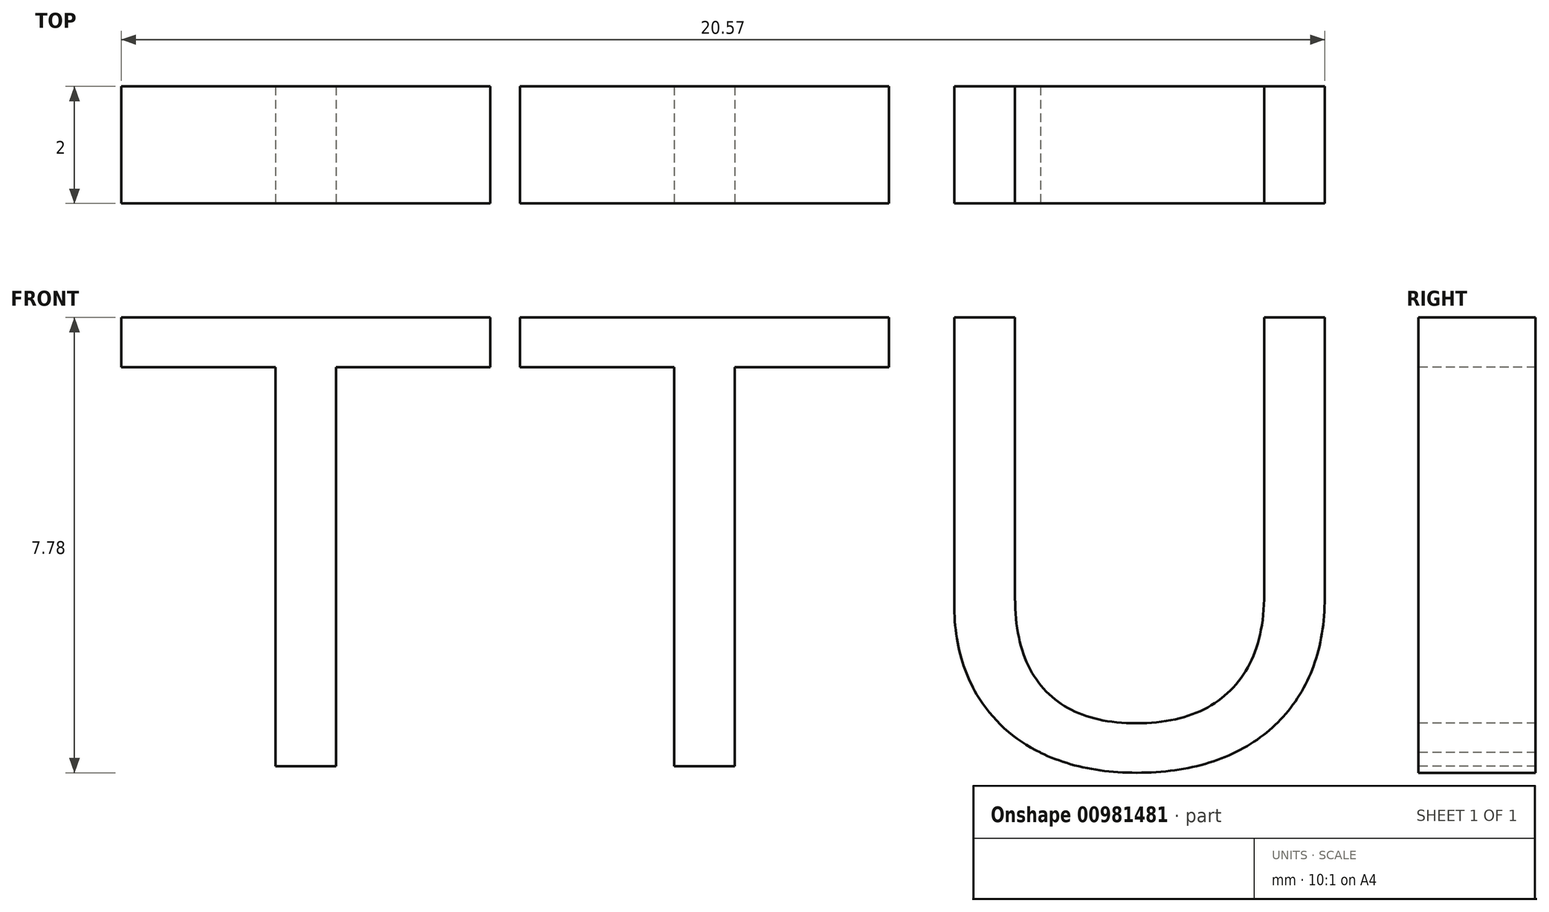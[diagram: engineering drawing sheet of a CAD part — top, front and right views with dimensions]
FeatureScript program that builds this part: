
annotation { "Feature Type Name" : "Feature", "Feature Type Description" : "" }
export const myFeature = defineFeature(function(context is Context, id is Id, definition is map)
    precondition{}
    {
        {
            var Q0;
            Q0=qCreatedBy(makeId("Front.planeOp"),FACE);
            var sketch = newSketch(context, id + "F0", { "sketchPlane" : qUnion([Q0])});
            skText(sketch, "E0", { "text": "TTU", "fontName": "Arimo-Regular.ttf"});
            const initialGuessF0  = {"E0": [-0.0064, 0.02997, 1, 0, 0.00803]};
            skSetInitialGuess(sketch, initialGuessF0);
            skSolve(sketch);
        }
        {
            var Q0;
            Q0=qSketchRegion(id+"F0",true);
            extrude(context, id + "F1", {"entities" : qUnion([Q0]), "oppositeDirection" : true, "depth" : 2 * mm, "offsetDistance" : 25 * mm});
        }
    });
